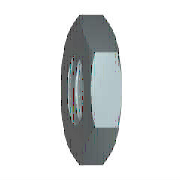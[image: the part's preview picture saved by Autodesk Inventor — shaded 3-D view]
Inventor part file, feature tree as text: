
AUTODESK INVENTOR PART (.ipt)
format: ipt  version: 2021 (Build 250183000, 183)  size: 169,472 bytes
history: native  units: mm (DEFAULTED — no unit token found)
features: sketch x3, chamfer x1, hole x1, other x1, plane x1
ambient origin geometry x7: Origin, YZ Plane, XZ Plane, X Axis, Y Axis, Z Axis, Center Point
bodies: Solid1 (feature_tree), Body (feature_tree)
feature tree (7):
  chamfer  "Chamfer1"  Angle=30.0deg  [1 undecoded]
  hole  "Thread"  [1 undecoded]
  other  "Work Axis1"
  plane  "Work Plane1"
  sketch  "Sketch1"  dims[d0=9.237604mm]
  sketch  "Sketch2"  dims[d1=2.7mm]
  sketch  "Sketch3"  dims[d2=0.0mm d3=30.0deg d4=30.0deg d5=6.9mm d6=6.9mm d7=90.0deg d25=4.134mm d26=6.0mm d27=4.0mm d28=2.0mm d29=14.3117mm d30=8.0mm d31=20.594885mm d8=0.433013mm d9=30.0deg d10=0.433013mm d11=30.0deg d13=0.0mm d14=0.0mm d39=0.0mm d40=0.433013mm d41=0.433013mm d42=0.0mm]
note: 2 required parameter values undecoded (feature->parameter linkage not recoverable at this tier; creation-order binding heuristic only, values carry confidence <= 0.55)
